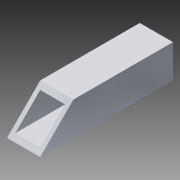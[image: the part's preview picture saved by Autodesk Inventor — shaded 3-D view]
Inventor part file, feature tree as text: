
AUTODESK INVENTOR PART (.ipt)
format: ipt  version: 2015 SP1 (Build 190203100, 203)  size: 104,448 bytes
history: native  units: in
note: dims shown in document units (in); Inventor stores cm internally (conversion verified against a paired STEP export)
features: extrude x2, sketch x2
ambient origin geometry x8: Origin, YZ Plane, XZ Plane, XY Plane, X Axis, Y Axis, Z Axis, Center Point
bodies: Solid1 (feature_tree)
feature tree (4):
  extrude  "Extrusion1"  Depth=1.0in
  extrude  "Extrusion2"  Depth=0.75in
  sketch  "Sketch1"  dims[d0=1.0in d1=1.0in]
  sketch  "Sketch2"  dims[d2=0.75in d3=0.75in d4=0.125in d5=0.125in d6=4.0in d7=0.0in d8=135.0deg d9=3.0in d10=0.0in]
